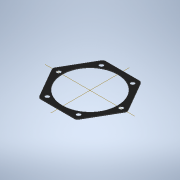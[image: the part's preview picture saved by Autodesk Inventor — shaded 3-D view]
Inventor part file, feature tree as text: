
AUTODESK INVENTOR PART (.ipt)
format: ipt  version: 2021.1 (Build 251245000, 245)  size: 141,824 bytes
history: native  units: in
note: dims shown in document units (in); Inventor stores cm internally (conversion verified against a paired STEP export)
features: extrude x1, sketch x1
ambient origin geometry x8: Origin, YZ Plane, XZ Plane, XY Plane, X Axis, Y Axis, Z Axis, Center Point
bodies: Solid1 (feature_tree)
feature tree (2):
  extrude  "Extrusion1"  Depth=0.5in
  sketch  "Sketch1"  dims[d0=10.6in d1=0.5in d2=10.2in d3=9.0in d4=0.7in d5=2.3622in d7=360.0deg d9=0.1in d10=0.0in]
